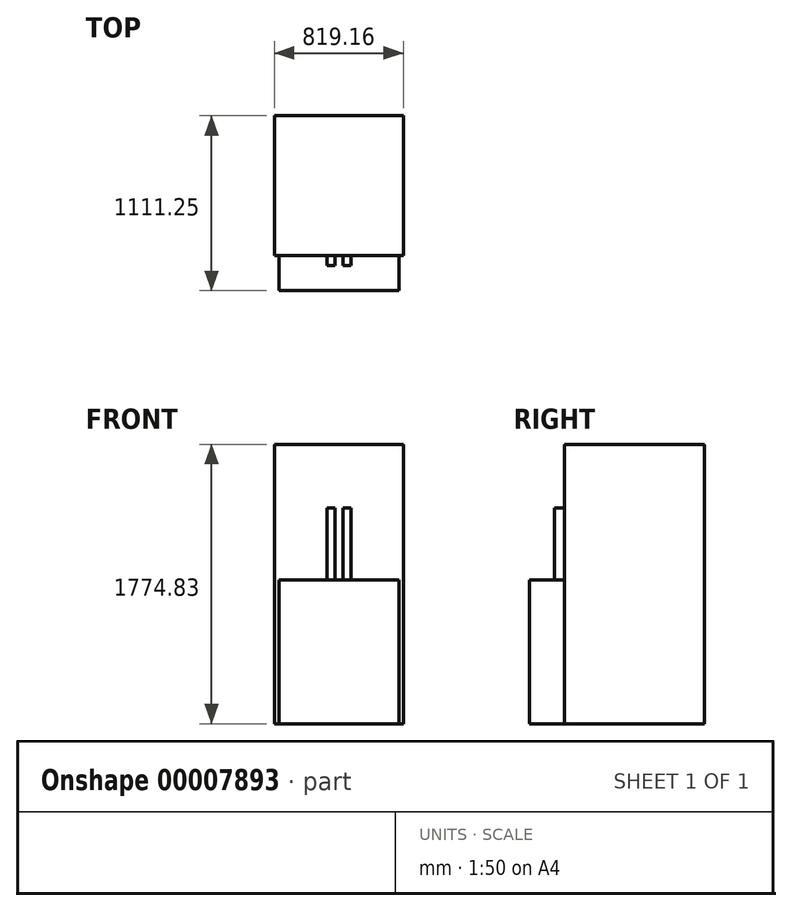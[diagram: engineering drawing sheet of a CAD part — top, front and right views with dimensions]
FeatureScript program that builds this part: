
annotation { "Feature Type Name" : "Feature", "Feature Type Description" : "" }
export const myFeature = defineFeature(function(context is Context, id is Id, definition is map)
    precondition{}
    {
        {
            var Q0;
            Q0=qCreatedBy(makeId("Right.planeOp"),FACE);
            var sketch = newSketch(context, id + "F0", { "sketchPlane" : qUnion([Q0])});
            skLineSegment(sketch, "E0", {"start": v(0, 0) * mm, "end": v(0, 1200.15) * mm});
            skLineSegment(sketch, "E1", {"start": v(0, 1200.15) * mm, "end": v(-76.2, 1200.15) * mm});
            skLineSegment(sketch, "E2", {"start": v(-76.2, 1200.15) * mm, "end": v(-76.2, 914.4) * mm});
            skLineSegment(sketch, "E3", {"start": v(-76.2, 914.4) * mm, "end": v(-666.75, 914.4) * mm});
            skLineSegment(sketch, "E4", {"start": v(-666.75, 914.4) * mm, "end": v(-666.75, 0) * mm});
            skLineSegment(sketch, "E5", {"start": v(-666.75, 0) * mm, "end": v(0, 0) * mm});
            skSolve(sketch);
        }
        {
            var Q0;
            Q0=makeQuery(id+"F0.imprint","IMPRINT",FACE,{"disambiguationData":[TD([[makeQuery(id+"F0.imprint","IMPRINT",EDGE,{"derivedFrom":sQuery(id+"F0.wireOp",EDGE,"E0")}),1.0]])]});
            extrude(context, id + "F1", {"entities" : qUnion([Q0]), "depth" : 762 * mm, "offsetDistance" : 25.4 * mm, "symmetric" : true});
        }
        {
            var Q0;
            Q0=qCreatedBy(makeId("Right.planeOp"),FACE);
            var sketch = newSketch(context, id + "F2", { "sketchPlane" : qUnion([Q0])});
            skLineSegment(sketch, "E6.bottom", {"start": v(-304.8, 876.3) * mm, "end": v(304.8, 876.3) * mm});
            skLineSegment(sketch, "E6.top", {"start": v(-304.8, 0) * mm, "end": v(304.8, 0) * mm});
            skLineSegment(sketch, "E6.left", {"start": v(-304.8, 876.3) * mm, "end": v(-304.8, 0) * mm});
            skLineSegment(sketch, "E6.right", {"start": v(304.8, 876.3) * mm, "end": v(304.8, 0) * mm});
            skSolve(sketch);
        }
        {
            var Q0;
            Q0 = qSketchRegion(id + "F2", true);
            extrude(context, id + "F3", {"entities" : qUnion([Q0]), "depth" : 762 * mm, "offsetDistance" : 25.4 * mm, "symmetric" : true});
        }
        {
            var Q0;
            Q0=makeQuery(id+"F3.opExtrude","SWEPT_FACE",FACE,{"disambiguationData":[OSD([sQuery(id+"F2.wireOp",EDGE,"E6.left")])]});
            var sketch = newSketch(context, id + "F4", { "sketchPlane" : qUnion([Q0])});
            skLineSegment(sketch, "E7.bottom", {"start": v(-304.8, 863.6) * mm, "end": v(304.8, 863.6) * mm});
            skLineSegment(sketch, "E7.top", {"start": v(-304.8, 812.8) * mm, "end": v(304.8, 812.8) * mm});
            skLineSegment(sketch, "E7.left", {"start": v(-304.8, 863.6) * mm, "end": v(-304.8, 812.8) * mm});
            skLineSegment(sketch, "E7.right", {"start": v(304.8, 863.6) * mm, "end": v(304.8, 812.8) * mm});
            skLineSegment(sketch, "E8", {"start": v(0, 812.8) * mm, "end": v(0, 0) * mm, "construction": true});
            skSolve(sketch);
        }
        {
            var Q0;
            Q0 = qSketchRegion(id + "F4", true);
            extrude(context, id + "F5", {"entities" : qUnion([Q0]), "operationType" : NewBodyOperationType.ADD, "depth" : 63.5 * mm, "offsetDistance" : 25.4 * mm});
        }
        {
            var Q0;
            Q0=qCreatedBy(makeId("Top.planeOp"),FACE);
            var sketch = newSketch(context, id + "F6", { "sketchPlane" : qUnion([Q0])});
            skLineSegment(sketch, "E9.bottom", {"start": v(409.57, -444.5) * mm, "end": v(-409.58, -444.5) * mm});
            skLineSegment(sketch, "E9.top", {"start": v(409.57, 444.5) * mm, "end": v(-409.58, 444.5) * mm});
            skLineSegment(sketch, "E9.left", {"start": v(409.57, -444.5) * mm, "end": v(409.58, 444.5) * mm});
            skLineSegment(sketch, "E9.right", {"start": v(-409.58, -444.5) * mm, "end": v(-409.58, 444.5) * mm});
            skPoint(sketch, "E9.middle", {"position": v(0, 0) * mm});
            skSolve(sketch);
        }
        {
            var Q0;
            Q0 = qSketchRegion(id + "F6", true);
            extrude(context, id + "F7", {"entities" : qUnion([Q0]), "depth" : 1774.82 * mm, "offsetDistance" : 25.4 * mm});
        }
        {
            var Q0;
            Q0=makeQuery(id+"F7.opExtrude","SWEPT_FACE",FACE,{"disambiguationData":[OSD([sQuery(id+"F6.wireOp",EDGE,"E9.bottom")])]});
            var sketch = newSketch(context, id + "F8", { "sketchPlane" : qUnion([Q0])});
            skLineSegment(sketch, "E10.bottom", {"start": v(25.4, 1371.6) * mm, "end": v(76.2, 1371.6) * mm});
            skLineSegment(sketch, "E10.top", {"start": v(25.4, 762) * mm, "end": v(76.2, 762) * mm});
            skLineSegment(sketch, "E10.left", {"start": v(25.4, 1371.6) * mm, "end": v(25.4, 762) * mm});
            skLineSegment(sketch, "E10.right", {"start": v(76.2, 1371.6) * mm, "end": v(76.2, 762) * mm});
            skLineSegment(sketch, "E11.bottom", {"start": v(-304.8, 431.8) * mm, "end": v(304.8, 431.8) * mm});
            skLineSegment(sketch, "E11.top", {"start": v(-304.8, 381) * mm, "end": v(304.8, 381) * mm});
            skLineSegment(sketch, "E11.left", {"start": v(-304.8, 431.8) * mm, "end": v(-304.8, 381) * mm});
            skLineSegment(sketch, "E11.right", {"start": v(304.8, 431.8) * mm, "end": v(304.8, 381) * mm});
            skLineSegment(sketch, "E12", {"start": v(0, 0) * mm, "end": v(0, 381) * mm, "construction": true});
            skLineSegment(sketch, "E13.MirrorCS", {"start": v(-25.4, 762) * mm, "end": v(-76.2, 762) * mm});
            skLineSegment(sketch, "E14.MirrorCS", {"start": v(-25.4, 1371.6) * mm, "end": v(-25.4, 762) * mm});
            skLineSegment(sketch, "E15.MirrorCS", {"start": v(-76.2, 1371.6) * mm, "end": v(-76.2, 762) * mm});
            skLineSegment(sketch, "E16.MirrorCS", {"start": v(-25.4, 1371.6) * mm, "end": v(-76.2, 1371.6) * mm});
            skSolve(sketch);
        }
        {
            var Q0;
            Q0 = qSketchRegion(id + "F8", true);
            extrude(context, id + "F9", {"entities" : qUnion([Q0]), "operationType" : NewBodyOperationType.ADD, "depth" : 63.5 * mm, "offsetDistance" : 25.4 * mm});
        }
    });
